# Revit family: Unico DE_Anta Doppia
name_source: partatom
category: Doors
revit_build: Autodesk Revit 2018 (Build: 20170223_1515(x64)
units: mm (PartAtom-declared; Revit-internal decimal feet)

## family parameters
Always vertical = Yes
Cut with Voids When Loaded = No
Host = Wall
OmniClass Number = 23.30.10.00
OmniClass Title = Doors
Room Calculation Point = Yes
Shared = No

## types (18) — shared parameters
AUTORE BIM = SKEIN BIM
Analytic Construction = <Nessuno>
DIMENSIONI DISPONIBILI = https://www.eclisse.it
DOOR DIMENSIONS = For the exact door panel width DW, please refer to the technical data sheet
Function = Interior
IFC Classification = Door
ISTRUZIONI INSTALLAZIONE = https://www.eclisse.it
Manufacturer = ECLISSE
Masterformat 2014 Code = 08 10 00
Masterformat 2014 Description = Doors and Frames
Model = ECLISSE UNICO
NBS Reference Code = 59-23
NBS Reference Description = Doorsets
OmniClass Code = 23-17 11 00
OmniClass Description = Doors
SCHEDA PRODOTTO = https://www.eclisse.it
SCHEDA TECNICA = https://www.eclisse.it
UNSPSC Code = 301715
URL = https://www.eclisse.it
Uniclass 1.4 Code = L411
Uniclass 1.4 Description = Doors
Uniclass 2.0 Description = Doorsets
Uniclass 2015 Code = EF_25_30
Uniclass 2015 Name = Doors and windows
Uniformat II Code = C1020
Uniformat II Description = Interior Doors
VOCE DI CAPITOLATO = https://www.eclisse.it
Wall Closure = By host

## per-type parameters (varying)
| type | A | B | C | H1 | HP | Height | L | LP | Rough Height | Rough Width | Thickness | Width | X |
| 1110X1985 | 2250 mm | 1110 mm  [stored 3.64173 ft] | 4480 mm | 2065 mm  [stored 6.77493 ft] | 1985 mm  [stored 6.51247 ft] | 1975 mm  [stored 6.47966 ft] | 2205 mm  [stored 7.23425 ft] | 1123 mm | 2014 mm | 686 mm | 44 mm | 2240 mm | 466 mm |
| 1235X1985 | 2500 mm | 1235 mm  [stored 4.05184 ft] | 4980 mm | 2065 mm  [stored 6.77493 ft] | 1985 mm  [stored 6.51247 ft] | 1975 mm  [stored 6.47966 ft] | 2455 mm | 1248 mm | 2014 mm | 686 mm | 44 mm | 2490 mm | 466 mm |
| 1110X2110 | 2250 mm | 1110 mm  [stored 3.64173 ft] | 4480 mm | 2190 mm  [stored 7.18504 ft] | 2110 mm  [stored 6.92257 ft] | 2100 mm | 2205 mm  [stored 7.23425 ft] | 1123 mm | 2116 mm | 584 mm | 44 mm | 2240 mm | 498 mm |
| 1110X2235 | 2250 mm | 1110 mm  [stored 3.64173 ft] | 4480 mm | 2315 mm | 2235 mm | 2225 mm | 2205 mm  [stored 7.23425 ft] | 1123 mm | 2420 mm | 584 mm | 40 mm  [stored 0.131234 ft] | 2240 mm | 529 mm |
| 1235X2110 | 2500 mm | 1235 mm  [stored 4.05184 ft] | 4980 mm | 2190 mm  [stored 7.18504 ft] | 2110 mm  [stored 6.92257 ft] | 2100 mm | 2455 mm | 1248 mm | 2014 mm | 686 mm | 44 mm | 2490 mm | 498 mm |
| 1235X2235 | 2500 mm | 1235 mm  [stored 4.05184 ft] | 4980 mm | 2315 mm | 2235 mm | 2225 mm | 2455 mm | 1248 mm | 2014 mm | 686 mm | 44 mm | 2490 mm | 529 mm |
| 610X1985 | 1250 mm  [stored 4.10105 ft] | 610 mm  [stored 2.00131 ft] | 2480 mm | 2065 mm  [stored 6.77493 ft] | 1985 mm  [stored 6.51247 ft] | 1975 mm  [stored 6.47966 ft] | 1205 mm  [stored 3.95341 ft] | 623 mm | 2014 mm | 686 mm | 44 mm | 1240 mm | 466 mm |
| 610X2110 | 1250 mm  [stored 4.10105 ft] | 610 mm  [stored 2.00131 ft] | 2480 mm | 2190 mm  [stored 7.18504 ft] | 2110 mm  [stored 6.92257 ft] | 2100 mm | 1205 mm  [stored 3.95341 ft] | 623 mm | 2014 mm | 686 mm | 44 mm | 1240 mm | 498 mm |
| 610X2235 | 1250 mm  [stored 4.10105 ft] | 610 mm  [stored 2.00131 ft] | 2480 mm | 2315 mm | 2235 mm | 2225 mm | 1205 mm  [stored 3.95341 ft] | 623 mm | 2014 mm | 686 mm | 44 mm | 1240 mm | 529 mm |
| 735X1985 | 1500 mm  [stored 4.92126 ft] | 735 mm | 2980 mm | 2065 mm  [stored 6.77493 ft] | 1985 mm  [stored 6.51247 ft] | 1975 mm  [stored 6.47966 ft] | 1455 mm  [stored 4.77362 ft] | 748 mm | 2014 mm | 686 mm | 44 mm | 1490 mm | 466 mm |
| 735X2110 | 1500 mm  [stored 4.92126 ft] | 735 mm | 2980 mm | 2190 mm  [stored 7.18504 ft] | 2110 mm  [stored 6.92257 ft] | 2100 mm | 1455 mm  [stored 4.77362 ft] | 748 mm | 2014 mm | 686 mm | 44 mm | 1490 mm | 498 mm |
| 735X2235 | 1500 mm  [stored 4.92126 ft] | 735 mm | 2980 mm | 2315 mm | 2235 mm | 2225 mm | 1455 mm  [stored 4.77362 ft] | 748 mm | 2014 mm | 686 mm | 44 mm | 1490 mm | 529 mm |
| 860X1985 | 1750 mm  [stored 5.74147 ft] | 860 mm | 3480 mm | 2065 mm  [stored 6.77493 ft] | 1985 mm  [stored 6.51247 ft] | 1975 mm  [stored 6.47966 ft] | 1705 mm  [stored 5.59383 ft] | 873 mm | 2014 mm | 686 mm | 44 mm | 1740 mm | 466 mm |
| 860X2110 | 1750 mm  [stored 5.74147 ft] | 860 mm | 3480 mm | 2190 mm  [stored 7.18504 ft] | 2110 mm  [stored 6.92257 ft] | 2100 mm | 1705 mm  [stored 5.59383 ft] | 873 mm | 2014 mm | 686 mm | 44 mm | 1740 mm | 498 mm |
| 860X2235 | 1750 mm  [stored 5.74147 ft] | 860 mm | 3480 mm | 2315 mm | 2235 mm | 2225 mm | 1705 mm  [stored 5.59383 ft] | 873 mm | 2014 mm | 686 mm | 44 mm | 1740 mm | 529 mm |
| 985X1985 | 2000 mm  [stored 6.56168 ft] | 985 mm  [stored 3.23163 ft] | 3980 mm | 2065 mm  [stored 6.77493 ft] | 1985 mm  [stored 6.51247 ft] | 1975 mm  [stored 6.47966 ft] | 1955 mm  [stored 6.41404 ft] | 998 mm | 2014 mm | 686 mm | 44 mm | 1990 mm | 466 mm |
| 985X2110 | 2000 mm  [stored 6.56168 ft] | 985 mm  [stored 3.23163 ft] | 3980 mm | 2190 mm  [stored 7.18504 ft] | 2110 mm  [stored 6.92257 ft] | 2100 mm | 1955 mm  [stored 6.41404 ft] | 998 mm | 2014 mm | 686 mm | 44 mm | 1990 mm | 498 mm |
| 985X2235 | 2000 mm  [stored 6.56168 ft] | 985 mm  [stored 3.23163 ft] | 3980 mm | 2315 mm | 2235 mm | 2225 mm | 1955 mm  [stored 6.41404 ft] | 998 mm | 2014 mm | 686 mm | 44 mm | 1990 mm | 529 mm |

note: [stored X ft] marks values corroborated as IEEE doubles in the binary element streams (Revit-internal decimal feet)

## geometry (parser evidence)
native form markers: Blend x4, Sweep x11
no freeform markers — native parametric forms only
